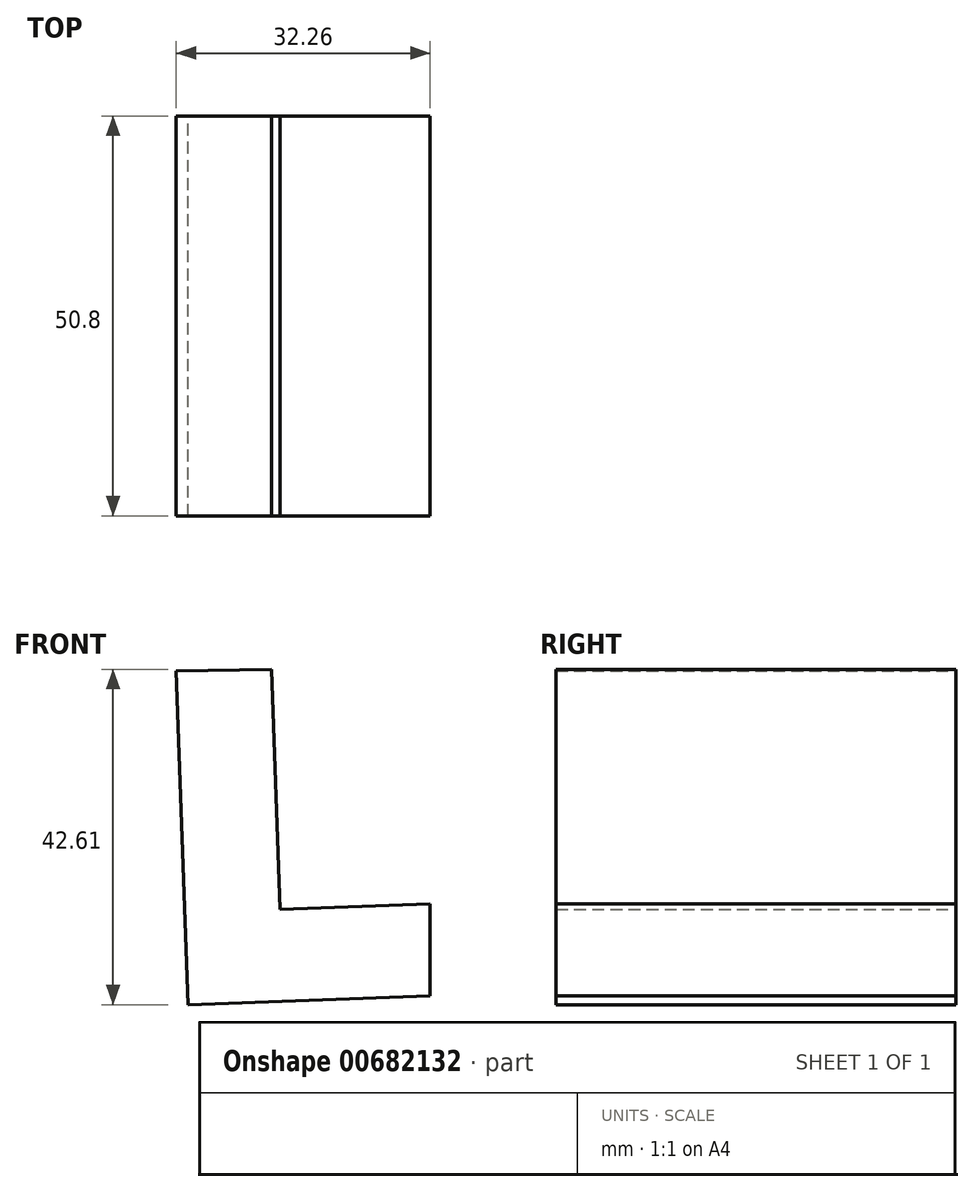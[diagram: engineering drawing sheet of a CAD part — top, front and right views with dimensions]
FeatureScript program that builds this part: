
annotation { "Feature Type Name" : "Feature", "Feature Type Description" : "" }
export const myFeature = defineFeature(function(context is Context, id is Id, definition is map)
    precondition{}
    {
        {
            var Q0;
            Q0=qCreatedBy(makeId("Front.planeOp"),FACE);
            var sketch = newSketch(context, id + "F0", { "sketchPlane" : qUnion([Q0])});
            skLineSegment(sketch, "E0", {"start": v(-54.33, 46.69) * mm, "end": v(-52.8, 4.3) * mm});
            skLineSegment(sketch, "E1", {"start": v(-52.8, 4.3) * mm, "end": v(-22.07, 5.4) * mm});
            skLineSegment(sketch, "E2", {"start": v(-22.07, 17.1) * mm, "end": v(-41.13, 16.4) * mm});
            skLineSegment(sketch, "E3", {"start": v(-41.13, 16.4) * mm, "end": v(-42.23, 46.9) * mm});
            skLineSegment(sketch, "E4", {"start": v(-42.23, 46.9) * mm, "end": v(-54.33, 46.69) * mm});
            skLineSegment(sketch, "E5", {"start": v(-22.07, 5.4) * mm, "end": v(-22.07, 17.1) * mm});
            skSolve(sketch);
        }
        {
            var Q0;
            Q0=makeQuery(id+"F0.imprint","IMPRINT",FACE,{"disambiguationData":[TD([[makeQuery(id+"F0.imprint","IMPRINT",EDGE,{"derivedFrom":sQuery(id+"F0.wireOp",EDGE,"E0")}),1.0]])]});
            extrude(context, id + "F1", {"entities" : qUnion([Q0]), "depth" : 50.8 * mm, "offsetDistance" : 25.4 * mm});
        }
    });
